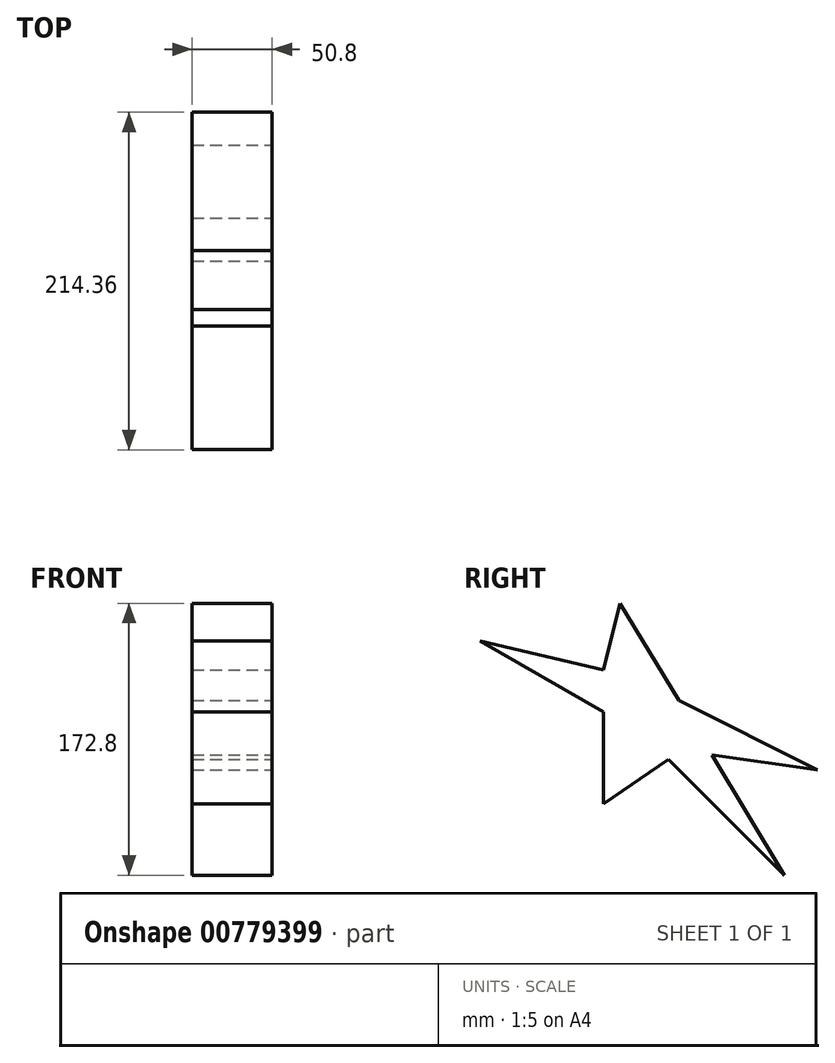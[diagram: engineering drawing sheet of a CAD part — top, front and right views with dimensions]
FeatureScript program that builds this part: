
annotation { "Feature Type Name" : "Feature", "Feature Type Description" : "" }
export const myFeature = defineFeature(function(context is Context, id is Id, definition is map)
    precondition{}
    {
        {
            var Q0;
            Q0=qCreatedBy(makeId("Right.planeOp"),FACE);
            var sketch = newSketch(context, id + "F0", { "sketchPlane" : qUnion([Q0])});
            skLineSegment(sketch, "E0", {"start": v(0, 0) * mm, "end": v(41.22, 28.26) * mm});
            skLineSegment(sketch, "E1", {"start": v(41.22, 28.26) * mm, "end": v(114.87, -45.38) * mm});
            skLineSegment(sketch, "E2", {"start": v(114.87, -45.38) * mm, "end": v(68.7, 31.02) * mm});
            skLineSegment(sketch, "E3", {"start": v(68.7, 31.02) * mm, "end": v(135.76, 21.6) * mm});
            skLineSegment(sketch, "E4", {"start": v(135.76, 21.6) * mm, "end": v(47.82, 65.58) * mm});
            skLineSegment(sketch, "E5", {"start": v(47.82, 65.58) * mm, "end": v(10.44, 127.42) * mm});
            skLineSegment(sketch, "E6", {"start": v(10.44, 127.42) * mm, "end": v(0, 85.15) * mm});
            skLineSegment(sketch, "E7", {"start": v(0, 85.15) * mm, "end": v(-78.6, 103.4) * mm});
            skLineSegment(sketch, "E8", {"start": v(-78.6, 103.4) * mm, "end": v(0, 58.32) * mm});
            skLineSegment(sketch, "E9", {"start": v(0, 58.32) * mm, "end": v(0, 0) * mm});
            skSolve(sketch);
        }
        {
            var Q0;
            Q0=makeQuery(id+"F0.imprint","IMPRINT",FACE,{"disambiguationData":[TD([[makeQuery(id+"F0.imprint","IMPRINT",EDGE,{"derivedFrom":sQuery(id+"F0.wireOp",EDGE,"E0")}),1.0]])]});
            extrude(context, id + "F1", {"entities" : qUnion([Q0]), "oppositeDirection" : true, "depth" : 50.8 * mm, "offsetDistance" : 25.4 * mm});
        }
    });
